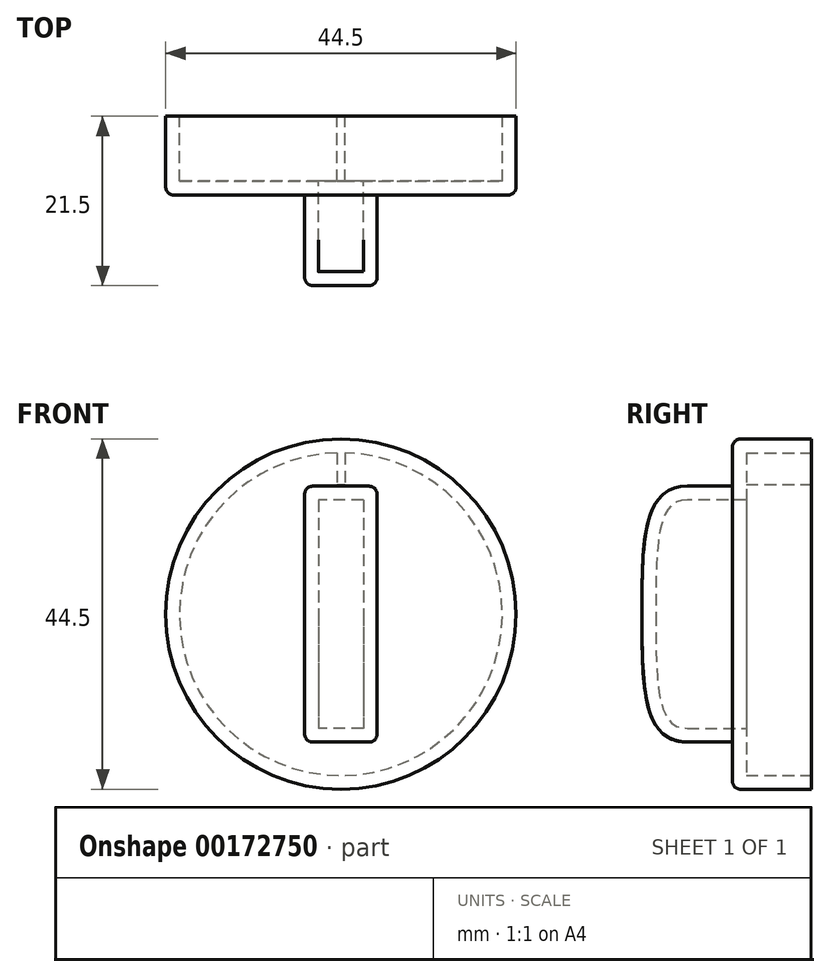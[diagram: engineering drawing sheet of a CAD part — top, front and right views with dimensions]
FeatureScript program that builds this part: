
annotation { "Feature Type Name" : "Feature", "Feature Type Description" : "" }
export const myFeature = defineFeature(function(context is Context, id is Id, definition is map)
    precondition{}
    {
        {
            var Q0;
            Q0=qCreatedBy(makeId("Front.planeOp"),FACE);
            var sketch = newSketch(context, id + "F0", { "sketchPlane" : qUnion([Q0])});
            skCircle(sketch, "E0", {"center": v(0, 0) * mm, "radius": 22.25 * mm});
            skSolve(sketch);
        }
        {
            var Q0;
            Q0=makeQuery(id+"F0.imprint","IMPRINT",FACE,{"disambiguationData":[TD([[makeQuery(id+"F0.imprint","IMPRINT",EDGE,{"derivedFrom":sQuery(id+"F0.wireOp",EDGE,"E0")}),1.0]])]});
            extrude(context, id + "F1", {"entities" : qUnion([Q0]), "depth" : 10 * mm});
        }
        {
            var Q0;
            Q0=makeQuery(id+"F1.opExtrude","CAP_FACE",FACE,{"disambiguationData":[OSD([sQuery(id+"F0.wireOp",EDGE,"E0")])],"isStart":false});
            var sketch = newSketch(context, id + "F2", { "sketchPlane" : qUnion([Q0])});
            skLineSegment(sketch, "E1.bottom", {"start": v(4.6, 16.25) * mm, "end": v(-4.6, 16.25) * mm});
            skLineSegment(sketch, "E1.top", {"start": v(4.6, -16.25) * mm, "end": v(-4.6, -16.25) * mm});
            skLineSegment(sketch, "E1.left", {"start": v(4.6, 16.25) * mm, "end": v(4.6, -16.25) * mm});
            skLineSegment(sketch, "E1.right", {"start": v(-4.6, 16.25) * mm, "end": v(-4.6, -16.25) * mm});
            skPoint(sketch, "E1.middle", {"position": v(0, 0) * mm});
            skSolve(sketch);
        }
        {
            var Q0;
            Q0=makeQuery(id+"F2.imprint","IMPRINT",FACE,{"disambiguationData":[TD([[makeQuery(id+"F2.imprint","IMPRINT",EDGE,{"derivedFrom":sQuery(id+"F2.wireOp",EDGE,"E1.bottom")}),1.0]])]});
            extrude(context, id + "F3", {"entities" : qUnion([Q0]), "operationType" : NewBodyOperationType.ADD, "depth" : 11.5 * mm});
        }
        {
            var Q0;
            Q0=makeQuery(id+"F3.opExtrude","SWEPT_FACE",FACE,{"disambiguationData":[OSD([sQuery(id+"F2.wireOp",EDGE,"E1.left")])]});
            var sketch = newSketch(context, id + "F4", { "sketchPlane" : qUnion([Q0])});
            skFitSpline(sketch, "E2", {"points": [v(-21.5, 0) * mm, v(-15.75, -16.25) * mm], "startDerivative": vector(0, -27.29) * mm, "endDerivative": vector(17.25, 0) * mm});
            skFitSpline(sketch, "E3.MirrorCS", {"points": [v(-21.5, 0) * mm, v(-15.75, 16.25) * mm], "startDerivative": vector(0, 27.29) * mm, "endDerivative": vector(17.25, 0) * mm});
            skSolve(sketch);
        }
        {
            var Q0;
            {var subQ0=sQuery(id+"F4.wireOp",EDGE,"E3.MirrorCS");Q0=makeQuery(id+"F4.imprint","IMPRINT",FACE,{"disambiguationData":[TD([[makeQuery(id+"F4.imprint","IMPRINT",EDGE,{"derivedFrom":subQ0}),1.0]])]});}
            var Q1;
            {var subQ0=sQuery(id+"F4.wireOp",EDGE,"E2");Q1=makeQuery(id+"F4.imprint","IMPRINT",FACE,{"disambiguationData":[TD([[makeQuery(id+"F4.imprint","IMPRINT",EDGE,{"derivedFrom":subQ0}),-1.0]])]});}
            extrude(context, id + "F5", {"entities" : qUnion([Q0, Q1]), "operationType" : NewBodyOperationType.REMOVE, "oppositeDirection" : true, "depth" : 10 * mm});
        }
        {
            var Q0;
            Q0=makeQuery(id+"F3.opExtrude","SWEPT_EDGE",EDGE,{"disambiguationData":[OSD([sQuery(id+"F2.wireOp",EDGE,"E1.top"),sQuery(id+"F2.wireOp",EDGE,"E1.left")])]});
            var Q1;
            Q1=makeQuery(id+"F5.boolean.opBoolean","INTERSECT",EDGE,{"derivedFrom":[makeQuery(id+"F3.opExtrude","SWEPT_FACE",FACE,{"disambiguationData":[OSD([sQuery(id+"F2.wireOp",EDGE,"E1.right")])]}),makeQuery(id+"F5.opExtrude","SWEPT_FACE",FACE,{"disambiguationData":[OSD([sQuery(id+"F4.wireOp",EDGE,"E2")])]})]});
            fillet(context, id + "F6", {"entities" : qUnion([Q0, Q1]), "radius" : 1 * mm, "tangentPropagation" : true, "allowEdgeOverflow" : false});
        }
        {
            var Q0;
            Q0=makeQuery(id+"F1.opExtrude","CAP_FACE",FACE,{"disambiguationData":[OSD([sQuery(id+"F0.wireOp",EDGE,"E0")])],"isStart":true});
            shell(context, id + "F7", {"entities" : qUnion([Q0]), "thickness" : 1.75 * mm});
        }
        {
            var Q0;
            Q0=qCreatedBy(makeId("Front.planeOp"),FACE);
            var sketch = newSketch(context, id + "F8", { "sketchPlane" : qUnion([Q0])});
            skLineSegment(sketch, "E4.bottom", {"start": v(0.5, 16.47) * mm, "end": v(-0.5, 16.47) * mm});
            skLineSegment(sketch, "E4.top", {"start": v(0.5, 20.57) * mm, "end": v(-0.5, 20.57) * mm});
            skLineSegment(sketch, "E4.left", {"start": v(0.5, 16.47) * mm, "end": v(0.5, 20.57) * mm});
            skLineSegment(sketch, "E4.right", {"start": v(-0.5, 16.47) * mm, "end": v(-0.5, 20.57) * mm});
            skPoint(sketch, "E4.middle", {"position": v(0, 18.52) * mm});
            skSolve(sketch);
        }
        {
            var Q0;
            {var subQ0=sQuery(id+"F8.wireOp",EDGE,"E4.bottom");Q0=makeQuery(id+"F8.imprint","IMPRINT",FACE,{"disambiguationData":[TD([[makeQuery(id+"F8.imprint","IMPRINT",EDGE,{"derivedFrom":subQ0}),-1.0]])]});}
            extrude(context, id + "F9", {"entities" : qUnion([Q0]), "operationType" : NewBodyOperationType.ADD, "depth" : 10 * mm});
        }
        {
            var Q0;
            Q0=makeQuery(id+"F1.opExtrude","CAP_EDGE",EDGE,{"disambiguationData":[OSD([sQuery(id+"F0.wireOp",EDGE,"E0")])],"isStart":false});
            fillet(context, id + "F10", {"entities" : qUnion([Q0]), "radius" : 1 * mm, "tangentPropagation" : true, "allowEdgeOverflow" : false});
        }
    });
